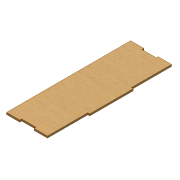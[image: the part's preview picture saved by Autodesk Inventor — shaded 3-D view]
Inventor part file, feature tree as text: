
AUTODESK INVENTOR PART (.ipt)
format: ipt  version: 2021 (Build 250183000, 183)  size: 111,616 bytes
history: native  units: mm
features: other x1, extrude x1, sketch x1
ambient origin geometry x8: Origin, YZ Plane, XZ Plane, XY Plane, X Axis, Y Axis, Z Axis, Center Point
bodies: Body1 (feature_tree)
feature tree (3):
  other  "Твердое тело1"
  extrude  "Выдавливание1"  Depth=4.0mm TaperAngle=0.0deg
  sketch  "Эскиз1"
